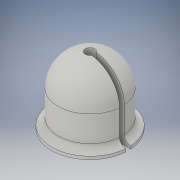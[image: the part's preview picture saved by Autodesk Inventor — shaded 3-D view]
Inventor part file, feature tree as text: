
AUTODESK INVENTOR PART (.ipt)
format: ipt  version: 2019 (Build 230136000, 136)  size: 186,880 bytes
history: native  units: in
note: dims shown in document units (in); Inventor stores cm internally (conversion verified against a paired STEP export)
features: sketch x4, extrude x2, revolve x1
ambient origin geometry x8: Origin, YZ Plane, XZ Plane, XY Plane, X Axis, Y Axis, Z Axis, Center Point
bodies: Solid1 (feature_tree)
feature tree (7):
  revolve  "Revolution1"  [1 undecoded]
  sketch  "Sketch2"  dims[d13=0.0394in d16=0.4134in]
  extrude  "Extrusion1"  Depth=0.0394in
  extrude  "Extrusion2"  Depth=0.1378in
  sketch  "Sketch1"  dims[d7=90.0deg d9=0.2362in]
  sketch  "Sketch3"  dims[d17=0.1969in d18=0.1378in]
  sketch  "Sketch4"  dims[d19=90.0deg d21=0.2165in d22=0.1969in d23=0.1378in d24=180.0deg d25=0.0591in d26=0.3937in d27=0.0in d28=0.0295in d29=0.3937in d30=0.0in]
note: 1 required parameter value undecoded (feature->parameter linkage not recoverable at this tier; creation-order binding heuristic only, values carry confidence <= 0.55)
